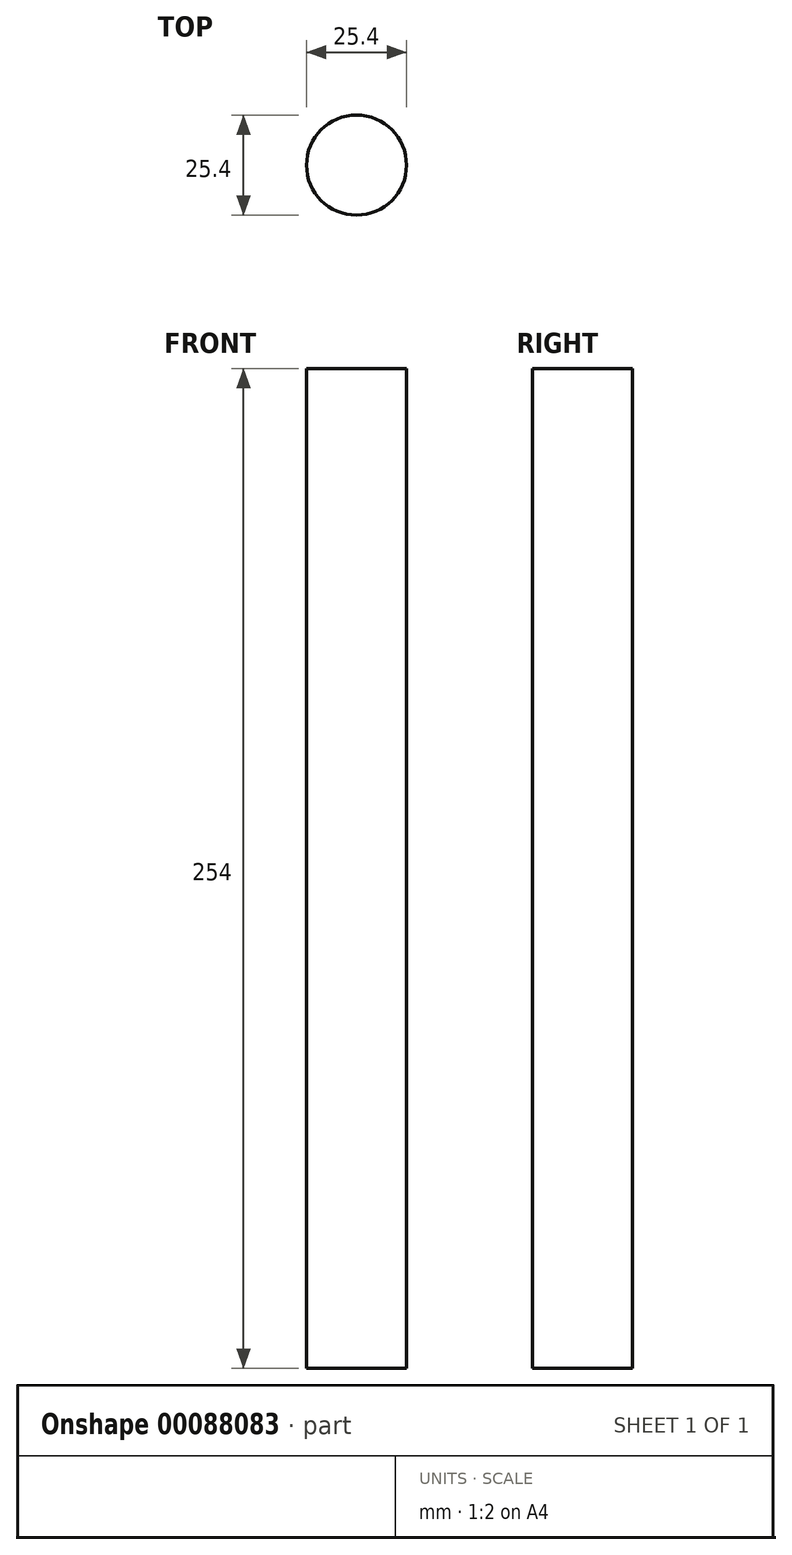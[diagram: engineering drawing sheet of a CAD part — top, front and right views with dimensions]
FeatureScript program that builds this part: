
annotation { "Feature Type Name" : "Feature", "Feature Type Description" : "" }
export const myFeature = defineFeature(function(context is Context, id is Id, definition is map)
    precondition{}
    {
        {
            var Q0;
            Q0=qCreatedBy(makeId("Top.planeOp"),FACE);
            var sketch = newSketch(context, id + "F0", { "sketchPlane" : qUnion([Q0])});
            skCircle(sketch, "E0", {"center": v(0, 0) * mm, "radius": 12.7 * mm});
            skSolve(sketch);
        }
        {
            var Q0;
            Q0 = qSketchRegion(id + "F0", true);
            extrude(context, id + "F1", {"entities" : qUnion([Q0]), "depth" : 254 * mm});
        }
    });
